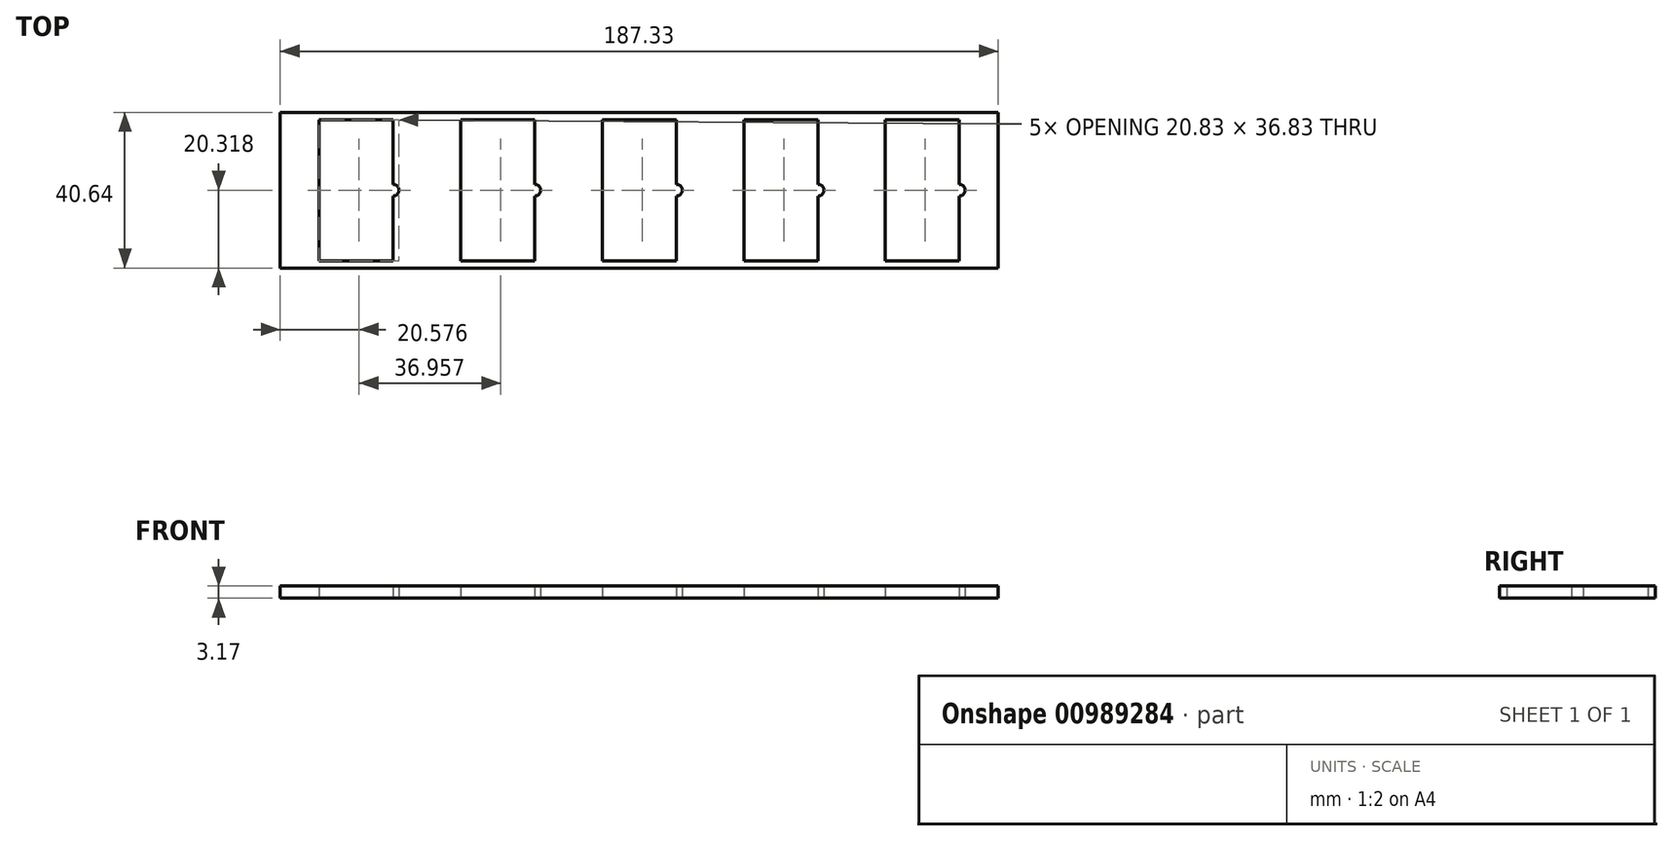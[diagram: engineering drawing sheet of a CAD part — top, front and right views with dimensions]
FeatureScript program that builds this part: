
annotation { "Feature Type Name" : "Feature", "Feature Type Description" : "" }
export const myFeature = defineFeature(function(context is Context, id is Id, definition is map)
    precondition{}
    {
        {
            var Q0;
            Q0=qCreatedBy(makeId("Top.planeOp"),FACE);
            var sketch = newSketch(context, id + "F0", { "sketchPlane" : qUnion([Q0])});
            skLineSegment(sketch, "E0.bottom", {"start": v(-43.58, 17.93) * mm, "end": v(143.75, 17.93) * mm});
            skLineSegment(sketch, "E0.top", {"start": v(-43.58, -22.71) * mm, "end": v(143.75, -22.71) * mm});
            skLineSegment(sketch, "E0.left", {"start": v(-43.58, 17.93) * mm, "end": v(-43.58, -22.71) * mm});
            skLineSegment(sketch, "E0.right", {"start": v(143.75, 17.93) * mm, "end": v(143.75, -22.71) * mm});
            skLineSegment(sketch, "E1.bottom", {"start": v(-33.42, 16.02) * mm, "end": v(-14.11, 16.02) * mm});
            skLineSegment(sketch, "E1.top", {"start": v(-33.42, -20.8) * mm, "end": v(-14.11, -20.8) * mm});
            skLineSegment(sketch, "E1.left", {"start": v(-33.42, 16.02) * mm, "end": v(-33.42, -20.8) * mm});
            skLineSegment(sketch, "E1.right", {"start": v(-14.11, 16.02) * mm, "end": v(-14.11, -20.8) * mm});
            skLineSegment(sketch, "E2.bottom", {"start": v(3.54, 16.02) * mm, "end": v(22.84, 16.02) * mm});
            skLineSegment(sketch, "E2.top", {"start": v(3.54, -20.8) * mm, "end": v(22.84, -20.8) * mm});
            skLineSegment(sketch, "E2.left", {"start": v(22.84, 16.02) * mm, "end": v(22.84, -20.8) * mm});
            skLineSegment(sketch, "E2.right", {"start": v(3.54, 16.02) * mm, "end": v(3.54, -20.8) * mm});
            skLineSegment(sketch, "E3.bottom", {"start": v(40.5, 16.02) * mm, "end": v(59.8, 16.02) * mm});
            skLineSegment(sketch, "E3.top", {"start": v(40.5, -20.8) * mm, "end": v(59.8, -20.8) * mm});
            skLineSegment(sketch, "E3.left", {"start": v(40.5, 16.02) * mm, "end": v(40.5, -20.8) * mm});
            skLineSegment(sketch, "E3.right", {"start": v(59.8, 16.02) * mm, "end": v(59.8, -20.8) * mm});
            skLineSegment(sketch, "E4.bottom", {"start": v(77.45, 16.02) * mm, "end": v(96.76, 16.02) * mm});
            skLineSegment(sketch, "E4.top", {"start": v(77.45, -20.8) * mm, "end": v(96.76, -20.8) * mm});
            skLineSegment(sketch, "E4.left", {"start": v(77.45, 16.02) * mm, "end": v(77.45, -20.8) * mm});
            skLineSegment(sketch, "E4.right", {"start": v(96.76, 16.02) * mm, "end": v(96.76, -20.8) * mm});
            skLineSegment(sketch, "E5.bottom", {"start": v(114.28, 16.02) * mm, "end": v(133.59, 16.02) * mm});
            skLineSegment(sketch, "E5.top", {"start": v(114.28, -20.8) * mm, "end": v(133.59, -20.8) * mm});
            skLineSegment(sketch, "E5.left", {"start": v(114.28, 16.02) * mm, "end": v(114.28, -20.8) * mm});
            skLineSegment(sketch, "E5.right", {"start": v(133.59, 16.02) * mm, "end": v(133.59, -20.8) * mm});
            skSolve(sketch);
        }
        {
            var Q0;
            Q0=makeQuery(id+"F0.imprint","IMPRINT",FACE,{"disambiguationData":[TD([[makeQuery(id+"F0.imprint","IMPRINT",EDGE,{"derivedFrom":sQuery(id+"F0.wireOp",EDGE,"E0.bottom")}),-1.0]])]});
            extrude(context, id + "F1", {"entities" : qUnion([Q0]), "depth" : 3.17 * mm});
        }
        {
            var Q0;
            Q0=makeQuery(id+"F1.opExtrude","CAP_FACE",FACE,{"disambiguationData":[OSD([sQuery(id+"F0.wireOp",EDGE,"E0.bottom"),sQuery(id+"F0.wireOp",EDGE,"E0.top"),sQuery(id+"F0.wireOp",EDGE,"E0.left"),sQuery(id+"F0.wireOp",EDGE,"E0.right"),sQuery(id+"F0.wireOp",EDGE,"E1.bottom"),sQuery(id+"F0.wireOp",EDGE,"E1.top"),sQuery(id+"F0.wireOp",EDGE,"E1.left"),sQuery(id+"F0.wireOp",EDGE,"E1.right"),sQuery(id+"F0.wireOp",EDGE,"E2.bottom"),sQuery(id+"F0.wireOp",EDGE,"E2.top"),sQuery(id+"F0.wireOp",EDGE,"E2.left"),sQuery(id+"F0.wireOp",EDGE,"E2.right"),sQuery(id+"F0.wireOp",EDGE,"E3.bottom"),sQuery(id+"F0.wireOp",EDGE,"E3.top"),sQuery(id+"F0.wireOp",EDGE,"E3.left"),sQuery(id+"F0.wireOp",EDGE,"E3.right"),sQuery(id+"F0.wireOp",EDGE,"E4.bottom"),sQuery(id+"F0.wireOp",EDGE,"E4.top"),sQuery(id+"F0.wireOp",EDGE,"E4.left"),sQuery(id+"F0.wireOp",EDGE,"E4.right"),sQuery(id+"F0.wireOp",EDGE,"E5.bottom"),sQuery(id+"F0.wireOp",EDGE,"E5.top"),sQuery(id+"F0.wireOp",EDGE,"E5.left"),sQuery(id+"F0.wireOp",EDGE,"E5.right")])],"isStart":false});
            var sketch = newSketch(context, id + "F2", { "sketchPlane" : qUnion([Q0])});
            skCircle(sketch, "E6", {"center": v(-14.11, -2.4) * mm, "radius": 1.52 * mm});
            skCircle(sketch, "E7", {"center": v(22.84, -2.4) * mm, "radius": 1.52 * mm});
            skCircle(sketch, "E8", {"center": v(59.8, -2.4) * mm, "radius": 1.52 * mm});
            skCircle(sketch, "E9", {"center": v(96.76, -2.4) * mm, "radius": 1.52 * mm});
            skCircle(sketch, "E10", {"center": v(133.59, -2.4) * mm, "radius": 1.52 * mm});
            skSolve(sketch);
        }
        {
            var Q0;
            Q0=qSketchRegion(id+"F2",true);
            extrude(context, id + "F3", {"entities" : qUnion([Q0]), "operationType" : NewBodyOperationType.REMOVE, "endBound" : BoundingType.SYMMETRIC, "depth" : 12.7 * mm});
        }
    });
